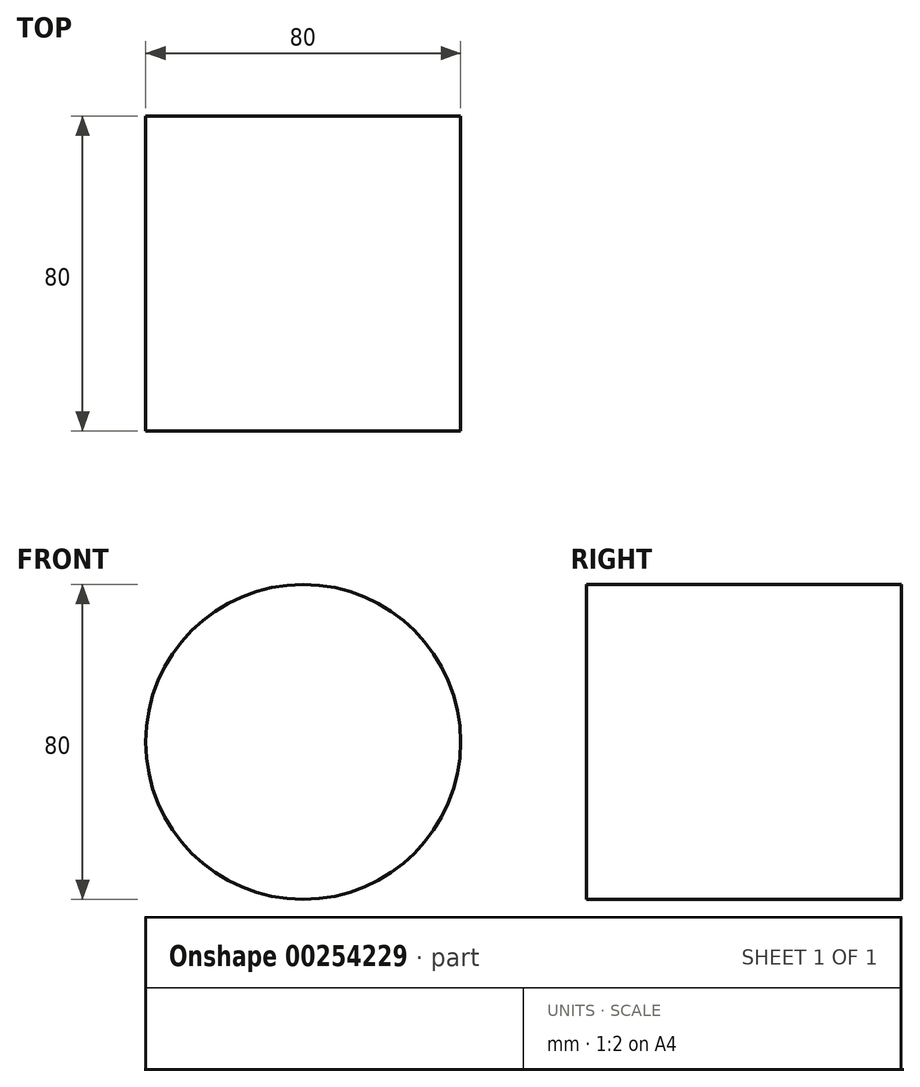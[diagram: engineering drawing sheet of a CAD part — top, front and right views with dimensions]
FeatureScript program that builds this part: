
annotation { "Feature Type Name" : "Feature", "Feature Type Description" : "" }
export const myFeature = defineFeature(function(context is Context, id is Id, definition is map)
    precondition{}
    {
        {
            var Q0;
            Q0=qCreatedBy(makeId("Front.planeOp"),FACE);
            var sketch = newSketch(context, id + "F0", { "sketchPlane" : qUnion([Q0])});
            skLineSegment(sketch, "E0", {"start": v(0, 0) * mm, "end": v(0, 91.54) * mm});
            skArc(sketch, "E1", {"start": v(0, 91.54) * mm, "mid": v(-40, 131.54) * mm, "end": v(-80, 91.54) * mm});
            skArc(sketch, "E2", {"start": v(0, 91.54) * mm, "mid": v(-40, 51.54) * mm, "end": v(-80, 91.54) * mm});
            skSolve(sketch);
        }
        {
            var Q0;
            Q0=makeQuery(id+"F0.imprint","IMPRINT",FACE,{"disambiguationData":[TD([[makeQuery(id+"F0.imprint","IMPRINT",EDGE,{"derivedFrom":sQuery(id+"F0.wireOp",EDGE,"E1")}),1.0]])]});
            extrude(context, id + "F1", {"entities" : qUnion([Q0]), "depth" : 80 * mm});
        }
    });
